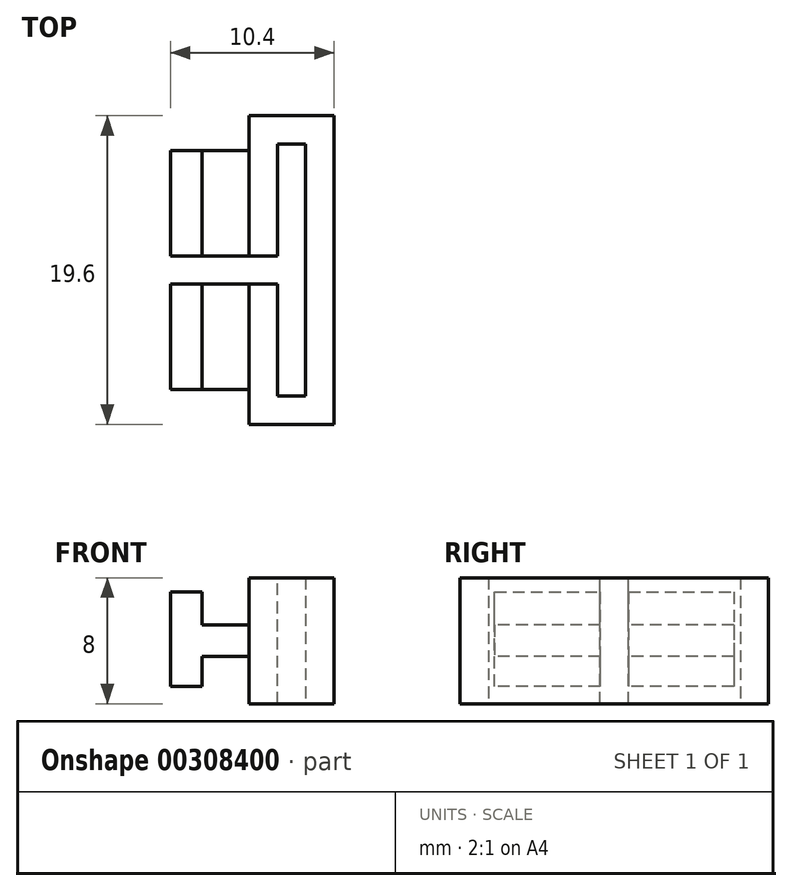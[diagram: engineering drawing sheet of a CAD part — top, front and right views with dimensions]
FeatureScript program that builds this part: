
annotation { "Feature Type Name" : "Feature", "Feature Type Description" : "" }
export const myFeature = defineFeature(function(context is Context, id is Id, definition is map)
    precondition{}
    {
        {
            var Q0;
            Q0=qCreatedBy(makeId("Top.planeOp"),FACE);
            var sketch = newSketch(context, id + "F0", { "sketchPlane" : qUnion([Q0])});
            skLineSegment(sketch, "E0.bottom", {"start": v(0.9, 8) * mm, "end": v(-0.9, 8) * mm});
            skLineSegment(sketch, "E0.top", {"start": v(0.9, -8) * mm, "end": v(-0.9, -8) * mm});
            skLineSegment(sketch, "E0.left", {"start": v(0.9, 8) * mm, "end": v(0.9, -8) * mm});
            skLineSegment(sketch, "E0.right", {"start": v(-0.9, 8) * mm, "end": v(-0.9, -8) * mm});
            skPoint(sketch, "E0.middle", {"position": v(0, 0) * mm});
            skLineSegment(sketch, "E1.bottom", {"start": v(2.7, 9.8) * mm, "end": v(-2.7, 9.8) * mm});
            skLineSegment(sketch, "E1.top", {"start": v(2.7, -9.8) * mm, "end": v(-2.7, -9.8) * mm});
            skLineSegment(sketch, "E1.left", {"start": v(2.7, 9.8) * mm, "end": v(2.7, -9.8) * mm});
            skLineSegment(sketch, "E1.right", {"start": v(-2.7, 9.8) * mm, "end": v(-2.7, -9.8) * mm});
            skSolve(sketch);
        }
        {
            var Q0;
            Q0=makeQuery(id+"F0.imprint","IMPRINT",FACE,{"disambiguationData":[TD([[makeQuery(id+"F0.imprint","IMPRINT",EDGE,{"derivedFrom":sQuery(id+"F0.wireOp",EDGE,"E0.bottom")}),-1.0]])]});
            extrude(context, id + "F1", {"entities" : qUnion([Q0]), "depth" : 8 * mm});
        }
        {
            var Q0;
            Q0=makeQuery(id+"F1.opExtrude","SWEPT_FACE",FACE,{"disambiguationData":[OSD([sQuery(id+"F0.wireOp",EDGE,"E1.right")])]});
            var sketch = newSketch(context, id + "F2", { "sketchPlane" : qUnion([Q0])});
            skLineSegment(sketch, "E2.bottom", {"start": v(-7.6, 5) * mm, "end": v(7.6, 5) * mm});
            skLineSegment(sketch, "E2.top", {"start": v(-7.6, 3) * mm, "end": v(7.6, 3) * mm});
            skLineSegment(sketch, "E2.left", {"start": v(-7.6, 5) * mm, "end": v(-7.6, 3) * mm});
            skLineSegment(sketch, "E2.right", {"start": v(7.6, 5) * mm, "end": v(7.6, 3) * mm});
            skPoint(sketch, "E2.middle", {"position": v(0, 4) * mm});
            skSolve(sketch);
        }
        {
            var Q0;
            Q0=makeQuery(id+"F2.imprint","IMPRINT",FACE,{"disambiguationData":[TD([[makeQuery(id+"F2.imprint","IMPRINT",EDGE,{"derivedFrom":sQuery(id+"F2.wireOp",EDGE,"E2.bottom")}),-1.0]])]});
            extrude(context, id + "F3", {"entities" : qUnion([Q0]), "operationType" : NewBodyOperationType.ADD, "offsetDistance" : 25 * mm, "depth" : 3 * mm});
        }
        {
            var Q0;
            Q0=makeQuery(id+"F3.opExtrude","CAP_FACE",FACE,{"disambiguationData":[OSD([sQuery(id+"F2.wireOp",EDGE,"E2.bottom"),sQuery(id+"F2.wireOp",EDGE,"E2.top"),sQuery(id+"F2.wireOp",EDGE,"E2.left"),sQuery(id+"F2.wireOp",EDGE,"E2.right")])],"isStart":false});
            var sketch = newSketch(context, id + "F4", { "sketchPlane" : qUnion([Q0])});
            skLineSegment(sketch, "E3", {"start": v(-7.6, 7.1) * mm, "end": v(-7.6, 1.1) * mm});
            skLineSegment(sketch, "E4", {"start": v(-7.6, 1.1) * mm, "end": v(7.6, 1.1) * mm});
            skLineSegment(sketch, "E5", {"start": v(7.6, 1.1) * mm, "end": v(7.6, 7.1) * mm});
            skLineSegment(sketch, "E6", {"start": v(7.6, 7.1) * mm, "end": v(-7.6, 7.1) * mm});
            skSolve(sketch);
        }
        {
            var Q0;
            Q0 = qSketchRegion(id + "F4", true);
            extrude(context, id + "F5", {"entities" : qUnion([Q0]), "operationType" : NewBodyOperationType.ADD, "depth" : 2 * mm});
        }
        {
            var Q0;
            Q0=makeQuery(id+"F1.opExtrude","CAP_FACE",FACE,{"disambiguationData":[OSD([sQuery(id+"F0.wireOp",EDGE,"E0.bottom"),sQuery(id+"F0.wireOp",EDGE,"E0.top"),sQuery(id+"F0.wireOp",EDGE,"E0.left"),sQuery(id+"F0.wireOp",EDGE,"E0.right"),sQuery(id+"F0.wireOp",EDGE,"E1.bottom"),sQuery(id+"F0.wireOp",EDGE,"E1.top"),sQuery(id+"F0.wireOp",EDGE,"E1.left"),sQuery(id+"F0.wireOp",EDGE,"E1.right")])],"isStart":false});
            var sketch = newSketch(context, id + "F6", { "sketchPlane" : qUnion([Q0])});
            skLineSegment(sketch, "E7.bottom", {"start": v(-0.9, 0.9) * mm, "end": v(-9.96, 0.9) * mm});
            skLineSegment(sketch, "E7.top", {"start": v(-0.9, -0.9) * mm, "end": v(-9.96, -0.9) * mm});
            skLineSegment(sketch, "E7.left", {"start": v(-0.9, 0.9) * mm, "end": v(-0.9, -0.9) * mm});
            skLineSegment(sketch, "E7.right", {"start": v(-9.96, 0.9) * mm, "end": v(-9.96, -0.9) * mm});
            skPoint(sketch, "E7.middle", {"position": v(-5.43, 0) * mm});
            skSolve(sketch);
        }
        {
            var Q0;
            Q0 = qSketchRegion(id + "F6", true);
            extrude(context, id + "F7", {"entities" : qUnion([Q0]), "operationType" : NewBodyOperationType.REMOVE, "endBound" : BoundingType.THROUGH_ALL, "oppositeDirection" : true, "depth" : 25 * mm});
        }
    });
